FCSTD DOCUMENT  (FreeCAD 0.18R14235 (Git))
Label: footprint-complex-arc-pads
License: All rights reserved
LicenseURL: http://en.wikipedia.org/wiki/All_rights_reserved
objects: Sketcher::SketchObject×10, Image::ImagePlane×2, App::Annotation×2, App::DocumentObjectGroup×1
note: 10 computed .brp shape members not serialized (recipe doc carries the construction recipe); baked Part::Feature solids carry a one-line shape summary decoded from their .brp

FEATURE [Image::ImagePlane] ImagePlane
  Placement = pos=(5.41,1.78,-2) rot=(0,0,1;0rad)
  XSize = 20.8258
  YSize = 8.73339
FEATURE [Sketcher::SketchObject] Sketch001  label="Pads_TH_SMD"
  sketch-geometry (12):
    g0: LineSegment StartX=-0.1425 StartY=1.875 StartZ=0 EndX=0.1425 EndY=1.875 EndZ=0
    g1: LineSegment StartX=0.1425 StartY=1.875 StartZ=0 EndX=0.1425 EndY=1.275 EndZ=0
    g2: LineSegment StartX=0.1425 StartY=1.275 StartZ=0 EndX=-0.1425 EndY=1.275 EndZ=0
    g3: LineSegment StartX=-0.1425 StartY=1.275 StartZ=0 EndX=-0.1425 EndY=1.875 EndZ=0
    g4: LineSegment StartX=-0.7425 StartY=1.875 StartZ=0 EndX=-0.4575 EndY=1.875 EndZ=0
    g5: LineSegment StartX=-0.4575 StartY=1.875 StartZ=0 EndX=-0.4575 EndY=1.275 EndZ=0
    g6: LineSegment StartX=-0.4575 StartY=1.275 StartZ=0 EndX=-0.7425 EndY=1.275 EndZ=0
    g7: LineSegment StartX=-0.7425 StartY=1.275 StartZ=0 EndX=-0.7425 EndY=1.875 EndZ=0
    g8: LineSegment StartX=0.7425 StartY=1.875 StartZ=0 EndX=0.4575 EndY=1.875 EndZ=0
    g9: LineSegment StartX=0.4575 StartY=1.875 StartZ=0 EndX=0.4575 EndY=1.275 EndZ=0
    g10: LineSegment StartX=0.4575 StartY=1.275 StartZ=0 EndX=0.7425 EndY=1.275 EndZ=0
    g11: LineSegment StartX=0.7425 StartY=1.275 StartZ=0 EndX=0.7425 EndY=1.875 EndZ=0
  constraints (28):
    c: Coincident(g0,g1)
    c: Coincident(g1,g2)
    c: Coincident(g2,g3)
    c: Coincident(g3,g0)
    c: Horizontal(g0)
    c: Horizontal(g2)
    c: Vertical(g1)
    c: Vertical(g3)
    c: Coincident(g4,g5)
    c: Coincident(g5,g6)
    c: Coincident(g6,g7)
    c: Coincident(g7,g4)
    c: Horizontal(g4)
    c: Horizontal(g6)
    c: Vertical(g5)
    c: Vertical(g7)
    c: DistanceY(g5,g5) = 0.6
    c: DistanceX(g6,g6) = 0.285
    c: DistanceX(g2,g2) = 0.285
    c: DistanceY(g1,g1) = 0.6
    c: Coincident(g8,g9)
    c: Coincident(g9,g10)
    c: Coincident(g10,g11)
    c: Coincident(g11,g8)
    c: Horizontal(g8)
    c: Horizontal(g10)
    c: Vertical(g9)
    c: Vertical(g11)
FEATURE [Sketcher::SketchObject] Sketch002  label="F_Silks_0.16"
  sketch-geometry (5):
    g0: LineSegment StartX=-0.95 StartY=2.06 StartZ=0 EndX=0.95 EndY=2.06 EndZ=0
    g1: LineSegment StartX=0.95 StartY=2.06 StartZ=0 EndX=0.95 EndY=-0.94 EndZ=0
    g2: LineSegment StartX=0.95 StartY=-0.94 StartZ=0 EndX=-0.95 EndY=-0.94 EndZ=0
    g3: LineSegment StartX=-0.95 StartY=-0.94 StartZ=0 EndX=-0.95 EndY=2.06 EndZ=0
    g4: LineSegment StartX=-0.75 StartY=2.06 StartZ=0 EndX=-0.95 EndY=1.7 EndZ=0
  constraints (16):
    c: Coincident(g0,g1)
    c: Coincident(g1,g2)
    c: Coincident(g2,g3)
    c: Coincident(g3,g0)
    c: Horizontal(g0)
    c: Horizontal(g2)
    c: Vertical(g1)
    c: Vertical(g3)
    c: DistanceX(g0,g0) = 1.9
    c: DistanceX(g-1,g1) = 0.95
    c: DistanceY(g1,g1) = 3
    c: DistanceX(g4,g0) = 0
    c: DistanceY(g0,g4) = 0
    c: DistanceY(g4,g0) = 0.36
    c: DistanceX(g0,g4) = 0.2
    c: DistanceY(g2,g-1) = 0.94
FEATURE [Image::ImagePlane] ImagePlane001
  Placement = pos=(-5.2,1.265,-2) rot=(0,0,1;0rad)
  XSize = 15.4997
  YSize = 6.49988
FEATURE [Sketcher::SketchObject] Sketch003  label="Pads_Poly"
  sketch-geometry (6):
    g0: LineSegment StartX=0.284196 StartY=0.377477 StartZ=0 EndX=0.463886 EndY=0.557167 EndZ=0
    g1: LineSegment [constr] StartX=0 StartY=0 StartZ=0 EndX=0.707924 EndY=0.707924 EndZ=0
    g2: LineSegment StartX=-0.284196 StartY=0.377477 StartZ=0 EndX=-0.463886 EndY=0.557167 EndZ=0
    g3: ArcOfCircle CenterX=0 CenterY=0 CenterZ=0 NormalX=0 NormalY=0 NormalZ=1 AngleXU=0 Radius=0.4725 StartAngle=0.925453 EndAngle=2.21614
    g4: ArcOfCircle CenterX=0 CenterY=0 CenterZ=0 NormalX=0 NormalY=0 NormalZ=1 AngleXU=0 Radius=0.725 StartAngle=0.876503 EndAngle=2.26509
    g5: Circle CenterX=0 CenterY=0.6 CenterZ=0 NormalX=0 NormalY=0 NormalZ=1 AngleXU=0 Radius=0.075
  constraints (5):
    c: Angle(g-1,g1) = 0.785398
    c: Parallel(g1,g0)
    c: PointOnObject(g4,g0)
    c: PointOnObject(g3,g0)
    c: Radius(g5) = 0.075
FEATURE [App::Annotation] Text  label="Ref#_0.8mm"
  LabelText = REF**
  Position = (0,2.5,0)
FEATURE [App::Annotation] Text001  label="Value#_0.8mm"
  LabelText = Value 
  Position = (0,-2,0)
FEATURE [Sketcher::SketchObject] Sketch004  label="Pads_NPTH"
  sketch-geometry (1):
    g0: Circle CenterX=0 CenterY=0 CenterZ=0 NormalX=0 NormalY=0 NormalZ=1 AngleXU=0 Radius=0.12
  constraints (2):
    c: Coincident(g0,g-1)
    c: Radius(g0) = 0.12
FEATURE [Sketcher::SketchObject] Sketch005  label="Pads_Poly1"
  sketch-geometry (8):
    g0: ArcOfCircle CenterX=0 CenterY=0 CenterZ=0 NormalX=0 NormalY=0 NormalZ=1 AngleXU=0 Radius=0.725 StartAngle=0 EndAngle=0.694293
    g1: ArcOfCircle CenterX=0 CenterY=0 CenterZ=0 NormalX=0 NormalY=0 NormalZ=1 AngleXU=0 Radius=0.4725 StartAngle=0 EndAngle=0.645344
    g2: LineSegment StartX=0.377477 StartY=0.284196 StartZ=0 EndX=0.557167 EndY=0.463886 EndZ=0
    g3: LineSegment [constr] StartX=0 StartY=0 StartZ=0 EndX=0.707924 EndY=0.707924 EndZ=0
    g4: LineSegment StartX=0.377477 StartY=-0.284196 StartZ=0 EndX=0.557167 EndY=-0.463886 EndZ=0
    g5: ArcOfCircle CenterX=0 CenterY=0 CenterZ=0 NormalX=0 NormalY=0 NormalZ=1 AngleXU=0 Radius=0.4725 StartAngle=5.63784 EndAngle=6.28319
    g6: ArcOfCircle CenterX=0 CenterY=0 CenterZ=0 NormalX=0 NormalY=0 NormalZ=1 AngleXU=0 Radius=0.725 StartAngle=5.58889 EndAngle=6.28319
    g7: Circle CenterX=0.6 CenterY=0 CenterZ=0 NormalX=0 NormalY=0 NormalZ=1 AngleXU=0 Radius=0.075
  constraints (12):
    c: Radius(g0) = 0.725
    c: DistanceY(g0,g0) = 0
    c: Radius(g1) = 0.4725
    c: DistanceY(g1,g1) = 0
    c: Coincident(g1,g0)
    c: Angle(g-1,g3) = 0.785398
    c: Coincident(g1,g2)
    c: Coincident(g0,g2)
    c: PointOnObject(g5,g4)
    c: PointOnObject(g6,g4)
    c: DistanceX(g0,g7) = 0.6
    c: DistanceY(g7,g0) = 0
FEATURE [Sketcher::SketchObject] Sketch006  label="Pads_Poly2"
  sketch-geometry (5):
    g0: LineSegment StartX=0.284196 StartY=-0.377477 StartZ=0 EndX=0.463886 EndY=-0.557167 EndZ=0
    g1: LineSegment StartX=-0.284196 StartY=-0.377477 StartZ=0 EndX=-0.463886 EndY=-0.557167 EndZ=0
    g2: ArcOfCircle CenterX=0 CenterY=0 CenterZ=0 NormalX=0 NormalY=0 NormalZ=1 AngleXU=0 Radius=0.4725 StartAngle=4.06705 EndAngle=5.35773
    g3: ArcOfCircle CenterX=0 CenterY=0 CenterZ=0 NormalX=0 NormalY=0 NormalZ=1 AngleXU=0 Radius=0.725 StartAngle=4.0181 EndAngle=5.40668
    g4: Circle CenterX=0 CenterY=-0.6 CenterZ=0 NormalX=0 NormalY=0 NormalZ=1 AngleXU=0 Radius=0.075
  constraints (5):
    c: PointOnObject(g2,g1)
    c: PointOnObject(g2,g0)
    c: PointOnObject(g3,g0)
    c: PointOnObject(g3,g1)
    c: Radius(g4) = 0.075
FEATURE [Sketcher::SketchObject] Sketch007  label="Pads_Poly3"
  sketch-geometry (7):
    g0: ArcOfCircle CenterX=0 CenterY=0 CenterZ=0 NormalX=0 NormalY=0 NormalZ=1 AngleXU=0 Radius=0.725 StartAngle=3.14159 EndAngle=3.83589
    g1: ArcOfCircle CenterX=0 CenterY=0 CenterZ=0 NormalX=0 NormalY=0 NormalZ=1 AngleXU=0 Radius=0.4725 StartAngle=3.14159 EndAngle=3.78694
    g2: LineSegment StartX=-0.377477 StartY=0.284196 StartZ=0 EndX=-0.557167 EndY=0.463886 EndZ=0
    g3: LineSegment StartX=-0.377477 StartY=-0.284196 StartZ=0 EndX=-0.557167 EndY=-0.463886 EndZ=0
    g4: ArcOfCircle CenterX=0 CenterY=0 CenterZ=0 NormalX=0 NormalY=0 NormalZ=1 AngleXU=0 Radius=0.4725 StartAngle=2.49625 EndAngle=3.14159
    g5: ArcOfCircle CenterX=0 CenterY=0 CenterZ=0 NormalX=0 NormalY=0 NormalZ=1 AngleXU=0 Radius=0.725 StartAngle=2.4473 EndAngle=3.14159
    g6: Circle CenterX=-0.6 CenterY=0 CenterZ=0 NormalX=0 NormalY=0 NormalZ=1 AngleXU=0 Radius=0.075
  constraints (6):
    c: Radius(g0) = 0.725
    c: Radius(g1) = 0.4725
    c: PointOnObject(g4,g2)
    c: PointOnObject(g5,g2)
    c: PointOnObject(g1,g3)
    c: PointOnObject(g0,g3)
FEATURE [Sketcher::SketchObject] Sketch009  label="Pads_Geom_0.25"
  sketch-geometry (2):
    g0: Circle CenterX=0 CenterY=0 CenterZ=0 NormalX=0 NormalY=0 NormalZ=1 AngleXU=0 Radius=0.6
    g1: Circle [constr] CenterX=0 CenterY=0.6 CenterZ=0 NormalX=0 NormalY=0 NormalZ=1 AngleXU=0 Radius=0.075
  constraints (5):
    c: Coincident(g0,g-1)
    c: Radius(g0) = 0.6
    c: Radius(g1) = 0.075
    c: Angle(g-1,g0) = 0.785398
    c: Distance(g1,g0) = 0.6
FEATURE [Sketcher::SketchObject] Sketch010  label="F_CrtYd_0.05"
  sketch-geometry (4):
    g0: LineSegment StartX=-0.95 StartY=2.06 StartZ=0 EndX=0.95 EndY=2.06 EndZ=0
    g1: LineSegment StartX=0.95 StartY=2.06 StartZ=0 EndX=0.95 EndY=-0.94 EndZ=0
    g2: LineSegment StartX=0.95 StartY=-0.94 StartZ=0 EndX=-0.95 EndY=-0.94 EndZ=0
    g3: LineSegment StartX=-0.95 StartY=-0.94 StartZ=0 EndX=-0.95 EndY=2.06 EndZ=0
  constraints (12):
    c: Coincident(g0,g1)
    c: Coincident(g1,g2)
    c: Coincident(g2,g3)
    c: Coincident(g3,g0)
    c: Horizontal(g0)
    c: Horizontal(g2)
    c: Vertical(g1)
    c: Vertical(g3)
    c: DistanceX(g0,g0) = 1.9
    c: DistanceX(g-1,g1) = 0.95
    c: DistanceY(g1,g1) = 3
    c: DistanceY(g2,g-1) = 0.94
FEATURE [Sketcher::SketchObject] Sketch011  label="F_Fab_0.1"
  sketch-geometry (5):
    g0: LineSegment StartX=-0.95 StartY=2.06 StartZ=0 EndX=0.95 EndY=2.06 EndZ=0
    g1: LineSegment StartX=0.95 StartY=2.06 StartZ=0 EndX=0.95 EndY=-0.94 EndZ=0
    g2: LineSegment StartX=0.95 StartY=-0.94 StartZ=0 EndX=-0.95 EndY=-0.94 EndZ=0
    g3: LineSegment StartX=-0.95 StartY=-0.94 StartZ=0 EndX=-0.95 EndY=2.06 EndZ=0
    g4: LineSegment StartX=-0.95 StartY=1.7 StartZ=0 EndX=-0.75 EndY=2.06 EndZ=0
  constraints (16):
    c: Coincident(g0,g1)
    c: Coincident(g1,g2)
    c: Coincident(g2,g3)
    c: Coincident(g3,g0)
    c: Horizontal(g0)
    c: Horizontal(g2)
    c: Vertical(g1)
    c: Vertical(g3)
    c: DistanceX(g0,g0) = 1.9
    c: DistanceX(g-1,g1) = 0.95
    c: DistanceY(g1,g1) = 3
    c: DistanceX(g4,g0) = 0
    c: DistanceY(g4,g0) = 0
    c: DistanceY(g4,g0) = 0.36
    c: DistanceX(g0,g4) = 0.2
    c: DistanceY(g2,g-1) = 0.94
FEATURE [App::DocumentObjectGroup] Group  label="fp-MEMS"
  Group = -> [Text,Text001,Sketch002,Sketch010,Sketch011,Sketch001,Sketch004,Sketch003,Sketch005,Sketch006,Sketch007,Sketch009]
